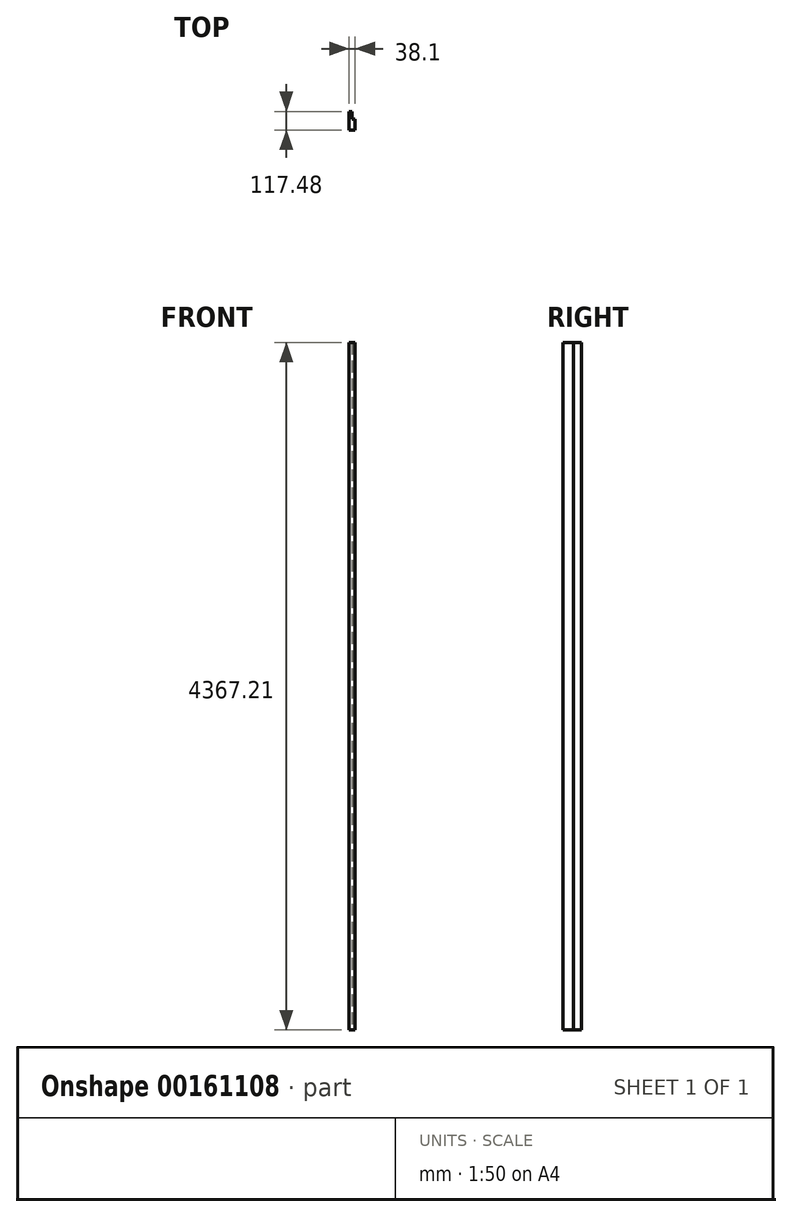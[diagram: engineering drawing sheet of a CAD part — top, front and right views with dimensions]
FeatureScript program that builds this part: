
annotation { "Feature Type Name" : "Feature", "Feature Type Description" : "" }
export const myFeature = defineFeature(function(context is Context, id is Id, definition is map)
    precondition{}
    {
        {
            var Q0;
            Q0=qCreatedBy(makeId("Top.planeOp"),FACE);
            var sketch = newSketch(context, id + "F0", { "sketchPlane" : qUnion([Q0])});
            skLineSegment(sketch, "E0", {"start": v(-2.14, 36.7) * mm, "end": v(-21.19, 36.7) * mm});
            skLineSegment(sketch, "E1", {"start": v(16.91, -80.78) * mm, "end": v(16.91, -12.52) * mm});
            skLineSegment(sketch, "E2", {"start": v(16.91, -12.52) * mm, "end": v(-2.14, -12.52) * mm});
            skLineSegment(sketch, "E3", {"start": v(-2.14, -12.52) * mm, "end": v(-2.14, 36.7) * mm});
            skLineSegment(sketch, "E4", {"start": v(-21.19, 36.7) * mm, "end": v(-21.19, -80.78) * mm});
            skLineSegment(sketch, "E5", {"start": v(-21.19, -80.78) * mm, "end": v(16.91, -80.78) * mm});
            skSolve(sketch);
        }
        {
            var Q0;
            Q0=qSketchRegion(id+"F0",true);
            extrude(context, id + "F1", {"entities" : qUnion([Q0]), "depth" : 4367.21 * mm});
        }
    });
